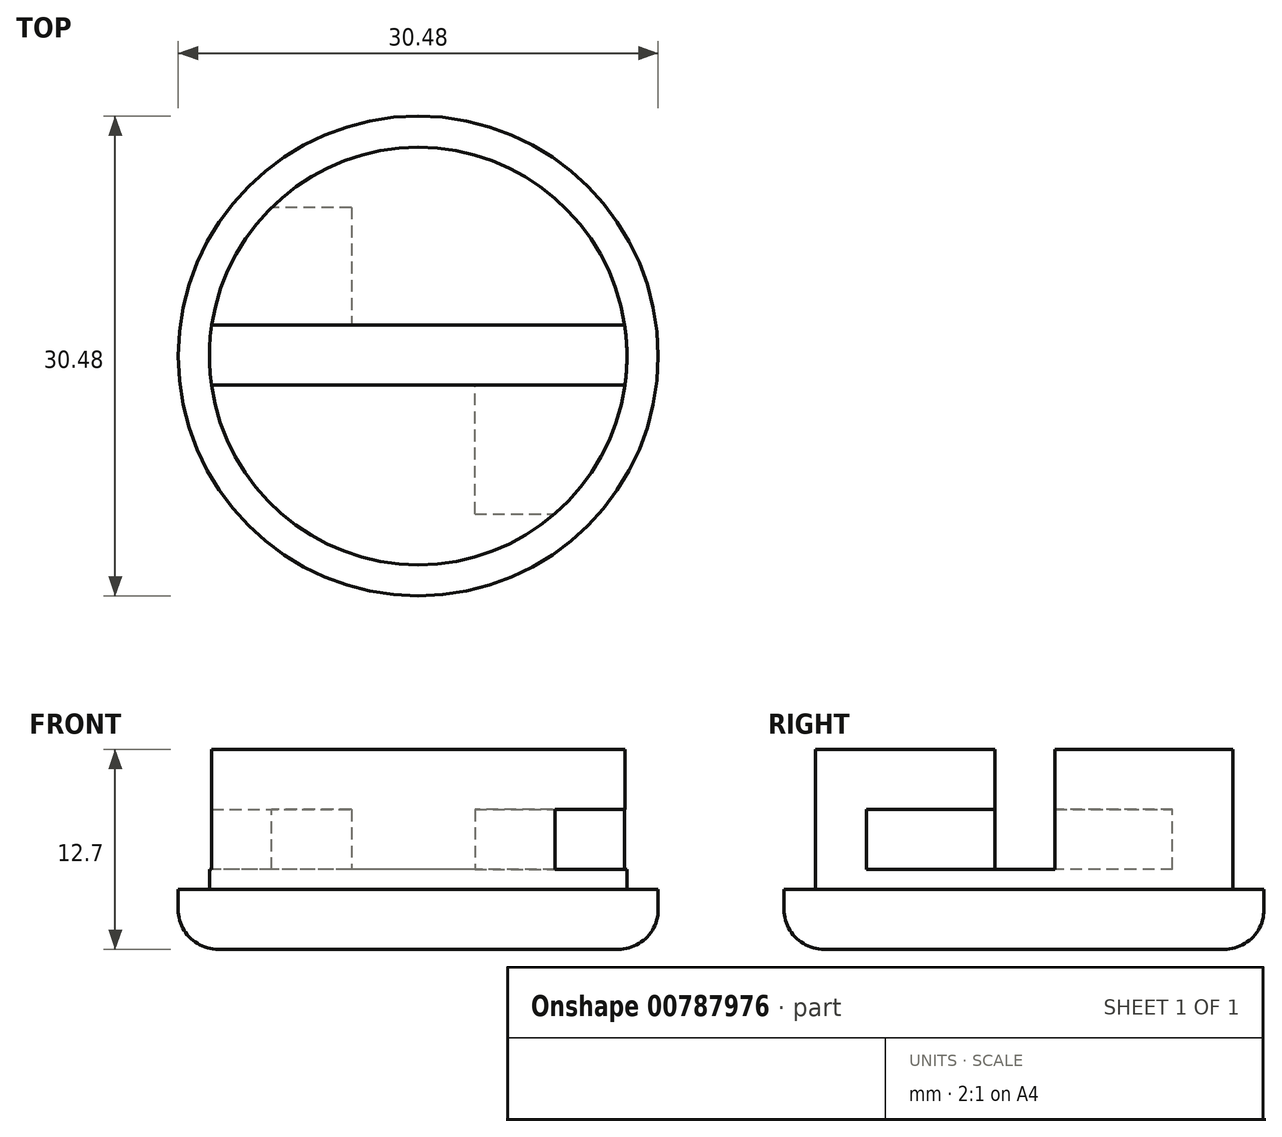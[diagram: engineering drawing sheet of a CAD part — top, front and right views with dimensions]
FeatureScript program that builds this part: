
annotation { "Feature Type Name" : "Feature", "Feature Type Description" : "" }
export const myFeature = defineFeature(function(context is Context, id is Id, definition is map)
    precondition{}
    {
        {
            var Q0;
            Q0=qCreatedBy(makeId("Top.planeOp"),FACE);
            var sketch = newSketch(context, id + "F0", { "sketchPlane" : qUnion([Q0])});
            skCircle(sketch, "E0", {"center": v(0, 0) * mm, "radius": 15.24 * mm});
            skSolve(sketch);
        }
        {
            var Q0;
            Q0 = qSketchRegion(id + "F0", true);
            extrude(context, id + "F1", {"entities" : qUnion([Q0]), "depth" : 12.7 * mm, "offsetDistance" : 25.4 * mm});
        }
        {
            var Q0;
            Q0=makeQuery(id+"F1.opExtrude","CAP_FACE",FACE,{"disambiguationData":[OSD([sQuery(id+"F0.wireOp",EDGE,"E0")])],"isStart":false});
            var sketch = newSketch(context, id + "F2", { "sketchPlane" : qUnion([Q0])});
            skCircle(sketch, "E1.0", {"center": v(0, 0) * mm, "radius": 13.26 * mm});
            skSolve(sketch);
        }
        {
            var Q0;
            Q0=makeQuery(id+"F2.imprint","IMPRINT",FACE,{"disambiguationData":[TD([[makeQuery(id+"F2.imprint","IMPRINT",EDGE,{"derivedFrom":sQuery(id+"F2.wireOp",EDGE,"E1.0")}),-1.0]])]});
            extrude(context, id + "F3", {"entities" : qUnion([Q0]), "operationType" : NewBodyOperationType.REMOVE, "oppositeDirection" : true, "depth" : 8.9 * mm, "offsetDistance" : 25.4 * mm});
        }
        {
            var Q0;
            Q0=makeQuery(id+"F1.opExtrude","CAP_FACE",FACE,{"disambiguationData":[OSD([sQuery(id+"F0.wireOp",EDGE,"E0")])],"isStart":false});
            var sketch = newSketch(context, id + "F4", { "sketchPlane" : qUnion([Q0])});
            skLineSegment(sketch, "E2.bottom", {"start": v(13.26, -1.85) * mm, "end": v(-13.26, -1.85) * mm});
            skLineSegment(sketch, "E2.top", {"start": v(13.26, 1.96) * mm, "end": v(-13.26, 1.96) * mm});
            skLineSegment(sketch, "E2.left", {"start": v(13.26, -1.85) * mm, "end": v(13.26, 1.96) * mm});
            skLineSegment(sketch, "E2.right", {"start": v(-13.26, -1.85) * mm, "end": v(-13.26, 1.96) * mm});
            skLineSegment(sketch, "E3", {"start": v(-13.26, 0) * mm, "end": v(13.26, 0) * mm});
            skLineSegment(sketch, "E4", {"start": v(13.26, 0) * mm, "end": v(13.26, 0) * mm});
            skSolve(sketch);
        }
        {
            var Q0;
            {var subQ0=sQuery(id+"F4.wireOp",EDGE,"E2.left");var subQ1=sQuery(id+"F4.wireOp",EDGE,"E2.bottom");var subQ2=makeQuery(id+"F4.imprint","INTERSECT",VERTEX,{"derivedFrom":[subQ1,subQ0]});Q0=makeQuery(id+"F4.imprint","IMPRINT",FACE,{"disambiguationData":[TD([[makeQuery(id+"F4.imprint","IMPRINT",EDGE,{"disambiguationData":[TD([[subQ2,-1.0]])],"derivedFrom":subQ1}),-1.0]])]});}
            var Q1;
            {var subQ0=sQuery(id+"F4.wireOp",EDGE,"E2.right");var subQ1=sQuery(id+"F4.wireOp",EDGE,"E2.bottom");var subQ2=makeQuery(id+"F4.imprint","INTERSECT",VERTEX,{"derivedFrom":[subQ1,subQ0]});Q1=makeQuery(id+"F4.imprint","IMPRINT",FACE,{"disambiguationData":[TD([[makeQuery(id+"F4.imprint","IMPRINT",EDGE,{"disambiguationData":[TD([[subQ2,1.0]])],"derivedFrom":subQ1}),-1.0]])]});}
            var Q2;
            {var subQ0=sQuery(id+"F4.wireOp",EDGE,"E2.left");var subQ1=sQuery(id+"F4.wireOp",EDGE,"E2.top");var subQ2=makeQuery(id+"F4.imprint","INTERSECT",VERTEX,{"derivedFrom":[subQ1,subQ0]});Q2=makeQuery(id+"F4.imprint","IMPRINT",FACE,{"disambiguationData":[TD([[makeQuery(id+"F4.imprint","IMPRINT",EDGE,{"disambiguationData":[TD([[subQ2,-1.0]])],"derivedFrom":subQ1}),1.0]])]});}
            var Q3;
            {var subQ0=sQuery(id+"F4.wireOp",EDGE,"E2.right");var subQ1=sQuery(id+"F4.wireOp",EDGE,"E2.top");var subQ2=makeQuery(id+"F4.imprint","INTERSECT",VERTEX,{"derivedFrom":[subQ1,subQ0]});Q3=makeQuery(id+"F4.imprint","IMPRINT",FACE,{"disambiguationData":[TD([[makeQuery(id+"F4.imprint","IMPRINT",EDGE,{"disambiguationData":[TD([[subQ2,1.0]])],"derivedFrom":subQ1}),1.0]])]});}
            var Q4;
            {var subQ4=sQuery(id+"F4.wireOp",EDGE,"E3");Q4=makeQuery(id+"F4.imprint","IMPRINT",FACE,{"disambiguationData":[TD([[makeQuery(id+"F4.imprint","IMPRINT",EDGE,{"derivedFrom":subQ4}),1.0]])]});}
            var Q5;
            {var subQ4=sQuery(id+"F4.wireOp",EDGE,"E3");Q5=makeQuery(id+"F4.imprint","IMPRINT",FACE,{"disambiguationData":[TD([[makeQuery(id+"F4.imprint","IMPRINT",EDGE,{"derivedFrom":subQ4}),-1.0]])]});}
            extrude(context, id + "F5", {"entities" : qUnion([Q0, Q1, Q2, Q3, Q4, Q5]), "operationType" : NewBodyOperationType.REMOVE, "oppositeDirection" : true, "depth" : 7.62 * mm, "offsetDistance" : 25.4 * mm});
        }
        {
            var Q0;
            Q0=makeQuery(id+"F5.boolean.opBoolean","COPY",FACE,{"derivedFrom":makeQuery(id+"F5.opExtrude","SWEPT_FACE",FACE,{"disambiguationData":[OSD([sQuery(id+"F4.wireOp",EDGE,"E2.bottom")])]})});
            var sketch = newSketch(context, id + "F6", { "sketchPlane" : qUnion([Q0])});
            skLineSegment(sketch, "E5", {"start": v(-13.13, 5.08) * mm, "end": v(-13.13, 8.89) * mm});
            skLineSegment(sketch, "E6", {"start": v(-13.13, 8.89) * mm, "end": v(-8.68, 8.89) * mm});
            skLineSegment(sketch, "E7", {"start": v(-8.68, 8.89) * mm, "end": v(-8.68, 5.08) * mm});
            skSolve(sketch);
        }
        {
            var Q0;
            {var subQ0=sQuery(id+"F6.wireOp",EDGE,"E5");Q0=makeQuery(id+"F6.imprint","IMPRINT",FACE,{"disambiguationData":[TD([[makeQuery(id+"F6.imprint","IMPRINT",EDGE,{"derivedFrom":subQ0}),-1.0]])]});}
            extrude(context, id + "F7", {"entities" : qUnion([Q0]), "operationType" : NewBodyOperationType.REMOVE, "oppositeDirection" : true, "depth" : 25.4 * mm, "offsetDistance" : 25.4 * mm});
        }
        {
            var Q0;
            Q0=makeQuery(id+"F5.boolean.opBoolean","COPY",FACE,{"derivedFrom":makeQuery(id+"F5.opExtrude","SWEPT_FACE",FACE,{"disambiguationData":[OSD([sQuery(id+"F4.wireOp",EDGE,"E2.top")])]})});
            var sketch = newSketch(context, id + "F8", { "sketchPlane" : qUnion([Q0])});
            skLineSegment(sketch, "E8", {"start": v(-13.11, 5.08) * mm, "end": v(-13.11, 8.89) * mm});
            skLineSegment(sketch, "E9", {"start": v(-13.11, 8.89) * mm, "end": v(-9.31, 8.89) * mm});
            skLineSegment(sketch, "E10", {"start": v(-9.31, 8.89) * mm, "end": v(-9.31, 5.08) * mm});
            skSolve(sketch);
        }
        {
            var Q0;
            {var subQ0=sQuery(id+"F8.wireOp",EDGE,"E8");Q0=makeQuery(id+"F8.imprint","IMPRINT",FACE,{"disambiguationData":[TD([[makeQuery(id+"F8.imprint","IMPRINT",EDGE,{"derivedFrom":subQ0}),1.0]])]});}
            extrude(context, id + "F9", {"entities" : qUnion([Q0]), "operationType" : NewBodyOperationType.REMOVE, "oppositeDirection" : true, "depth" : 25.4 * mm, "offsetDistance" : 25.4 * mm});
        }
        {
            var Q0;
            Q0=makeQuery(id+"F1.opExtrude","CAP_EDGE",EDGE,{"disambiguationData":[OSD([sQuery(id+"F0.wireOp",EDGE,"E0")])],"isStart":true});
            fillet(context, id + "F10", {"entities" : qUnion([Q0]), "radius" : 2.54 * mm, "tangentPropagation" : true, "allowEdgeOverflow" : false});
        }
        {
            var Q0;
            Q0=makeQuery(id+"F9.boolean.opBoolean","COPY",FACE,{"derivedFrom":makeQuery(id+"F9.opExtrude","SWEPT_FACE",FACE,{"disambiguationData":[OSD([sQuery(id+"F8.wireOp",EDGE,"E10")])]})});
            extrude(context, id + "F11", {"entities" : qUnion([Q0]), "operationType" : NewBodyOperationType.REMOVE, "oppositeDirection" : true, "depth" : 5.08 * mm, "offsetDistance" : 25.4 * mm});
        }
        {
            var Q0;
            Q0=makeQuery(id+"F7.boolean.opBoolean","COPY",FACE,{"derivedFrom":makeQuery(id+"F7.opExtrude","SWEPT_FACE",FACE,{"disambiguationData":[OSD([sQuery(id+"F6.wireOp",EDGE,"E7")])]})});
            extrude(context, id + "F12", {"entities" : qUnion([Q0]), "operationType" : NewBodyOperationType.REMOVE, "oppositeDirection" : true, "depth" : 5.08 * mm, "offsetDistance" : 25.4 * mm});
        }
    });
